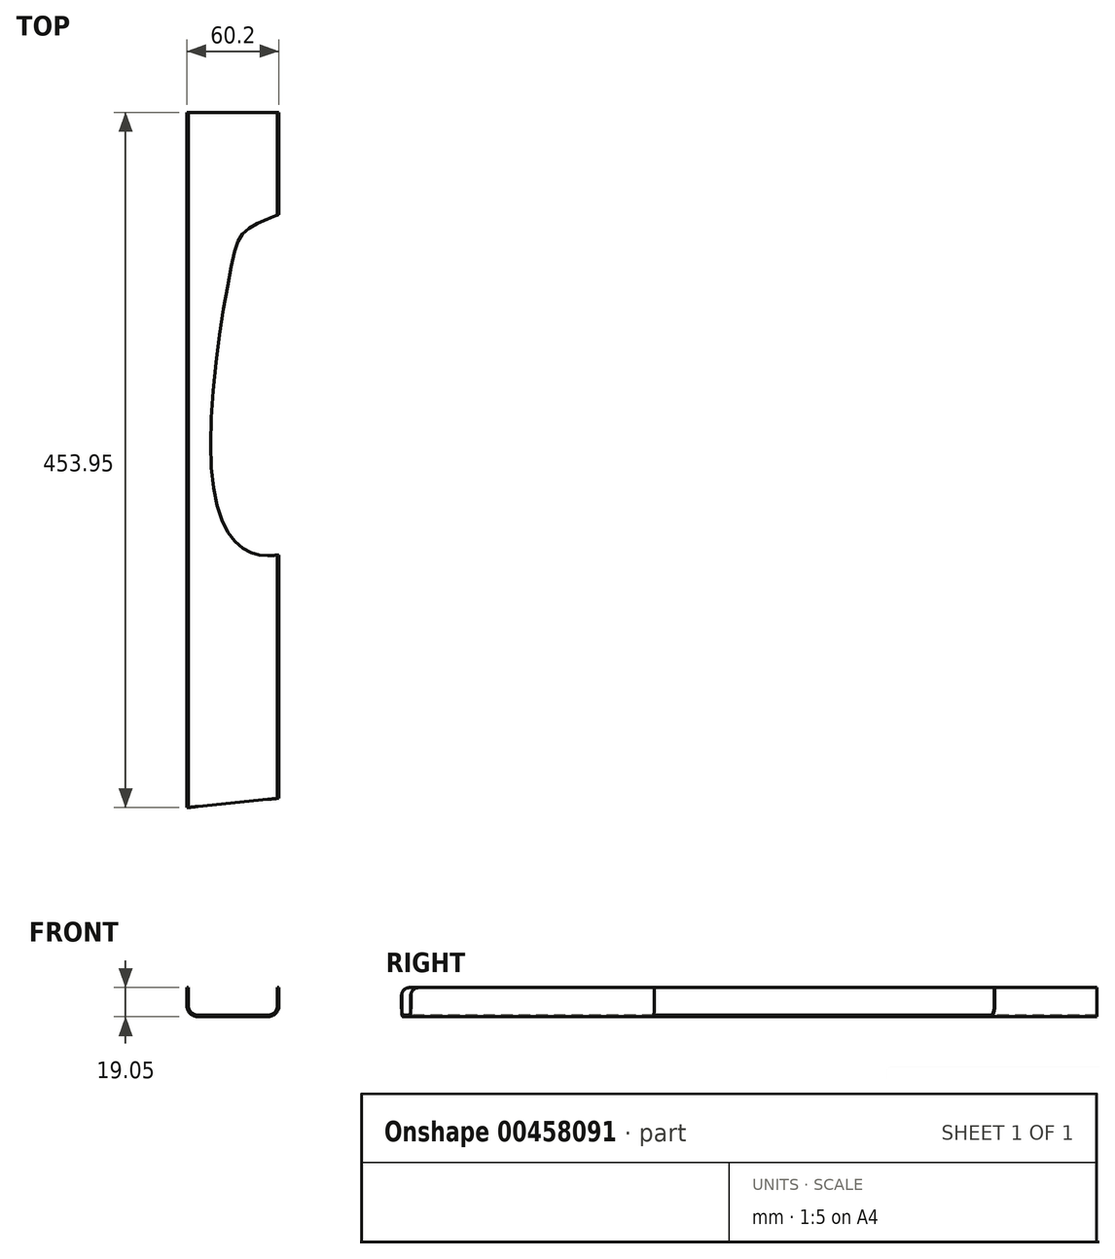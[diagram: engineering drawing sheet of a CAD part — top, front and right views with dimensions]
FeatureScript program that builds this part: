
annotation { "Feature Type Name" : "Feature", "Feature Type Description" : "" }
export const myFeature = defineFeature(function(context is Context, id is Id, definition is map)
    precondition{}
    {
        {
            var Q0;
            Q0=qCreatedBy(makeId("Front.planeOp"),FACE);
            var sketch = newSketch(context, id + "F0", { "sketchPlane" : qUnion([Q0])});
            skLineSegment(sketch, "E0.MirrorCS", {"start": v(29.08, 7.37) * mm, "end": v(29.08, 19.05) * mm});
            skLineSegment(sketch, "E1.MirrorCS", {"start": v(0, 1.02) * mm, "end": v(22.73, 1.02) * mm});
            skPoint(sketch, "E2.orphan", {"position": v(29.08, 0) * mm});
            skPoint(sketch, "E3.orphan", {"position": v(30.1, 1.02) * mm});
            skLineSegment(sketch, "E4", {"start": v(29.08, 19.05) * mm, "end": v(30.1, 19.05) * mm});
            skPoint(sketch, "E5.visualSharp", {"position": v(29.08, 1.02) * mm});
            skArc(sketch, "E5.filletArc", {"start": v(22.73, 1.02) * mm, "mid": v(27.22, 2.88) * mm, "end": v(29.08, 7.37) * mm});
            skArc(sketch, "E6.0", {"start": v(22.73, 0) * mm, "mid": v(27.94, 2.16) * mm, "end": v(30.1, 7.37) * mm});
            skLineSegment(sketch, "E7", {"start": v(30.1, 7.37) * mm, "end": v(30.1, 19.05) * mm});
            skLineSegment(sketch, "E8", {"start": v(22.73, 0) * mm, "end": v(0, 0) * mm});
            skLineSegment(sketch, "E9", {"start": v(0, 1.02) * mm, "end": v(0, 28.2) * mm});
            skLineSegment(sketch, "E10.MirrorCS", {"start": v(0, 1.02) * mm, "end": v(-22.73, 1.02) * mm});
            skLineSegment(sketch, "E11.MirrorCS", {"start": v(-22.73, 0) * mm, "end": v(0, 0) * mm});
            skArc(sketch, "E12.MirrorCS", {"start": v(-22.73, 0) * mm, "mid": v(-27.94, 2.16) * mm, "end": v(-30.1, 7.37) * mm});
            skArc(sketch, "E13.MirrorCS", {"start": v(-22.73, 1.02) * mm, "mid": v(-27.22, 2.88) * mm, "end": v(-29.08, 7.37) * mm});
            skLineSegment(sketch, "E14.MirrorCS", {"start": v(-29.08, 7.37) * mm, "end": v(-29.08, 19.05) * mm});
            skLineSegment(sketch, "E15.MirrorCS", {"start": v(-30.1, 7.37) * mm, "end": v(-30.1, 19.05) * mm});
            skLineSegment(sketch, "E16", {"start": v(-30.1, 19.05) * mm, "end": v(-29.08, 19.05) * mm});
            skSolve(sketch);
        }
        {
            var Q0;
            Q0 = qSketchRegion(id + "F0", true);
            extrude(context, id + "F1", {"entities" : qUnion([Q0]), "oppositeDirection" : true, "depth" : 454.02 * mm});
        }
        {
            var Q0;
            Q0=makeQuery(id+"F1.opExtrude","SWEPT_FACE",FACE,{"disambiguationData":[OSD([sQuery(id+"F0.wireOp",EDGE,"E8"),sQuery(id+"F0.wireOp",EDGE,"E11.MirrorCS")])]});
            var sketch = newSketch(context, id + "F2", { "sketchPlane" : qUnion([Q0])});
            skLineSegment(sketch, "E17", {"start": v(30.62, 0) * mm, "end": v(30.62, -6.35) * mm});
            skLineSegment(sketch, "E18", {"start": v(30.62, 0) * mm, "end": v(-30.9, 0) * mm});
            skLineSegment(sketch, "E19", {"start": v(-30.9, 0) * mm, "end": v(30.62, -6.25) * mm});
            skSolve(sketch);
        }
        {
            var Q0;
            Q0 = qSketchRegion(id + "F2", true);
            extrude(context, id + "F3", {"entities" : qUnion([Q0]), "operationType" : NewBodyOperationType.REMOVE, "endBound" : BoundingType.THROUGH_ALL, "oppositeDirection" : true, "depth" : 25.4 * mm, "hasSecondDirection" : true, "secondDirectionBound" : BoundingType.THROUGH_ALL, "secondDirectionOppositeDirection" : false, "secondDirectionDepth" : 25.4 * mm});
        }
        {
            var Q0;
            Q0=qCreatedBy(makeId("Top.planeOp"),FACE);
            var sketch = newSketch(context, id + "F4", { "sketchPlane" : qUnion([Q0])});
            skLineSegment(sketch, "E20", {"start": v(30, 387.35) * mm, "end": v(62.33, 387.35) * mm});
            skLineSegment(sketch, "E21", {"start": v(62.33, 387.35) * mm, "end": v(62.33, 165.98) * mm});
            skLineSegment(sketch, "E22", {"start": v(62.33, 165.98) * mm, "end": v(30, 165.1) * mm});
            skFitSpline(sketch, "E23", {"points": [v(30, 165.1) * mm, v(16.03, 165.1) * mm, v(0, 175.42) * mm, v(-14.44, 229.83) * mm, v(0, 358.03) * mm, v(8.7, 376.87) * mm, v(30, 387.35) * mm], "startDerivative": vector(-134.84, -14.92) * mm, "endDerivative": vector(183.52, 71.55) * mm});
            skSolve(sketch);
        }
        {
            var Q0;
            Q0 = qSketchRegion(id + "F4", true);
            extrude(context, id + "F5", {"entities" : qUnion([Q0]), "operationType" : NewBodyOperationType.REMOVE, "endBound" : BoundingType.THROUGH_ALL, "oppositeDirection" : true, "depth" : 25.4 * mm, "hasSecondDirection" : true, "secondDirectionBound" : BoundingType.THROUGH_ALL, "secondDirectionOppositeDirection" : false, "secondDirectionDepth" : 25.4 * mm});
        }
        {
            var Q0;
            Q0=makeQuery(id+"F3.boolean.opBoolean","INTERSECT",EDGE,{"derivedFrom":[makeQuery(id+"F1.opExtrude","SWEPT_FACE",FACE,{"disambiguationData":[OSD([sQuery(id+"F0.wireOp",EDGE,"E16")])]}),makeQuery(id+"F3.opExtrude","SWEPT_FACE",FACE,{"disambiguationData":[OSD([sQuery(id+"F2.wireOp",EDGE,"E19")])]})]});
            var Q1;
            Q1=makeQuery(id+"F3.boolean.opBoolean","INTERSECT",EDGE,{"derivedFrom":[makeQuery(id+"F1.opExtrude","SWEPT_FACE",FACE,{"disambiguationData":[OSD([sQuery(id+"F0.wireOp",EDGE,"E4")])]}),makeQuery(id+"F3.opExtrude","SWEPT_FACE",FACE,{"disambiguationData":[OSD([sQuery(id+"F2.wireOp",EDGE,"E19")])]})]});
            fillet(context, id + "F6", {"entities" : qUnion([Q0, Q1]), "radius" : 5.08 * mm, "allowEdgeOverflow" : false});
        }
    });
